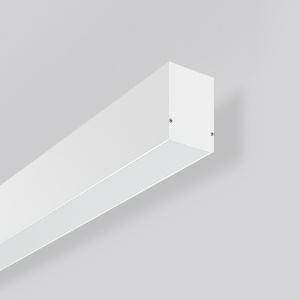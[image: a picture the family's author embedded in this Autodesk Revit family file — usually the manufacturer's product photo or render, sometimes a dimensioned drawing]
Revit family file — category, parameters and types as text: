
# Revit family: less_is_more_50_312607_002_76_a93d
name_source: partatom
category: Lighting Fixtures
units: mm (PartAtom-declared; Revit-internal decimal feet)

## family parameters
Cut with Voids When Loaded = No
Host = Face
Light Source = No
Part Type = Normal
Room Calculation Point = No
Round Connector Dimension = Use Diameter
Shared = No

## types (1)
- LESS IS MORE 50 (1 x LED Modul 830, 1450 lm, 3000)
    Apparent Load = 13 VA
    CIE Flux Codes = 48 80 96 100 100
    Color Rendering = 80
    Color Temperature = 3000
    Default Elevation = 1800 mm
    Description = Series: LESS IS MORE 50
Linear wall luminaires. Housing: extruded aluminium profile, powder-coated. End cap aluminium powder-coated. Diffuser made of non-yellowing plastic (PMMA), opal. Direct light emission. Suitable for Wall (surface). LED unit with integrated converter interchangeable and removable. Suitable for through-wiring. With sensors or as a safety luminaire on request. 
Colour: traffic white, matt (RAL 9016)
Length: 1127 mm
Width: 67 mm
Height: 75 mm
Lamp: LED
Socket: without socket
Colour temperature: 3000K
Colour rendering index (CRI): 80
System power: 13 W
Rated luminous flux: 1450 lm
Luminous efficiency: 112 lm/W
Control gear: Converter, dimmable, DALI
Protection class: I
Type of protection: IP 20
    Height = 75 mm
    Lamp = 1 x LED Modul 830
    Lamp Light Flux = 1450 lm
    Lamp count = 1
    Length = 1127 mm
    Lifetime = 50000 h
    Luminous efficacy = 112 lm/W
    Manufacturer = RZB
    ModVariant = No
    Model = 312607.002.76
    Mounting Place = Wall
    Mounting Type = Surface mounted
    Number of Poles = 1
    OnlyDefault = Yes
    Power Factor = 1
    Product Name = LESS IS MORE 50
    Product group = Surface mounted LED linear luminaires
    ProductGroupID = 2007
    Protection Class = Protection class I
    Protection Degree = IP 20
    RLX_Detail_Level = 1
    RLX_Emergency_Light_Flux = 0 lm
    RLX_Emergency_Type = 0
    RLX_Emergency_Type_DB = No
    RlxData = <blob elided: 35141 chars, md5=d10f0167>
    Socket = socket
    Standby Power = 0 W
    System Light Flux = 1450 lm
    System Power = 13 W
    Type Comments = Product without accessories
    Type Image = 312606.002.jpg
    URL = http://relux.com
    VarID = ---
    Voltage = 0 V
    Weight = 0.00 kg
    Width = 67 mm

## geometry (parser evidence)
native form markers: Blend x4, Sweep x9
no freeform markers — native parametric forms only
